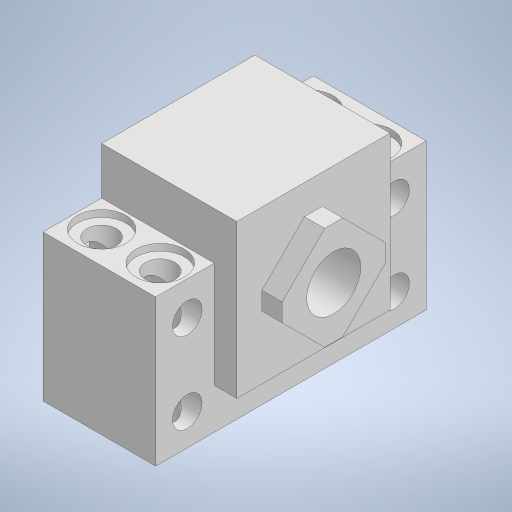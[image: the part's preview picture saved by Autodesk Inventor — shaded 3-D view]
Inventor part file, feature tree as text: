
AUTODESK INVENTOR PART (.ipt)
format: ipt  version: 2023 (Build 270158000, 158)  size: 311,296 bytes
history: native  units: mm
features: extrude x5, sketch x5, pattern_linear x1
ambient origin geometry x8: Origin, YZ Plane, XZ Plane, XY Plane, X Axis, Y Axis, Z Axis, Center Point
bodies: Solid1 (feature_tree)
feature tree (11):
  extrude  "Extrusion1"  Depth=60.0mm
  extrude  "Extrusion2"  Depth=46.0mm
  extrude  "Extrusion3"  Depth=32.5mm
  extrude  "Extrusion4"  Depth=43.0mm
  extrude  "Extrusion5"  Depth=25.0mm TaperAngle=0.0deg
  pattern_linear  "Rectangular Pattern1"  Spacing1=5.0mm  [1 undecoded]
  sketch  "Sketch1"  dims[d0=60.0mm d1=6.6mm]
  sketch  "Sketch2"  dims[d2=18.0mm d3=46.0mm]
  sketch  "Sketch3"  dims[d4=25.0mm d5=32.5mm]
  sketch  "Sketch4"  dims[d6=34.0mm d7=43.0mm]
  sketch  "Sketch5"  dims[d8=12.0mm d9=25.0mm d10=0.0mm d11=5.0mm d12=0.0mm d14=135.0deg d15=19.0mm d16=4.0mm d17=4.5mm d18=0.0mm d19=10.8mm d20=6.0mm d21=7.0mm d22=1.5mm d23=0.0mm d24=6.6mm d25=5.0mm d26=0.0mm d27=20.0mm d29=13.0mm d30=20.0mm d32=-46.0mm]
note: 1 required parameter value undecoded (feature->parameter linkage not recoverable at this tier; creation-order binding heuristic only, values carry confidence <= 0.55)
